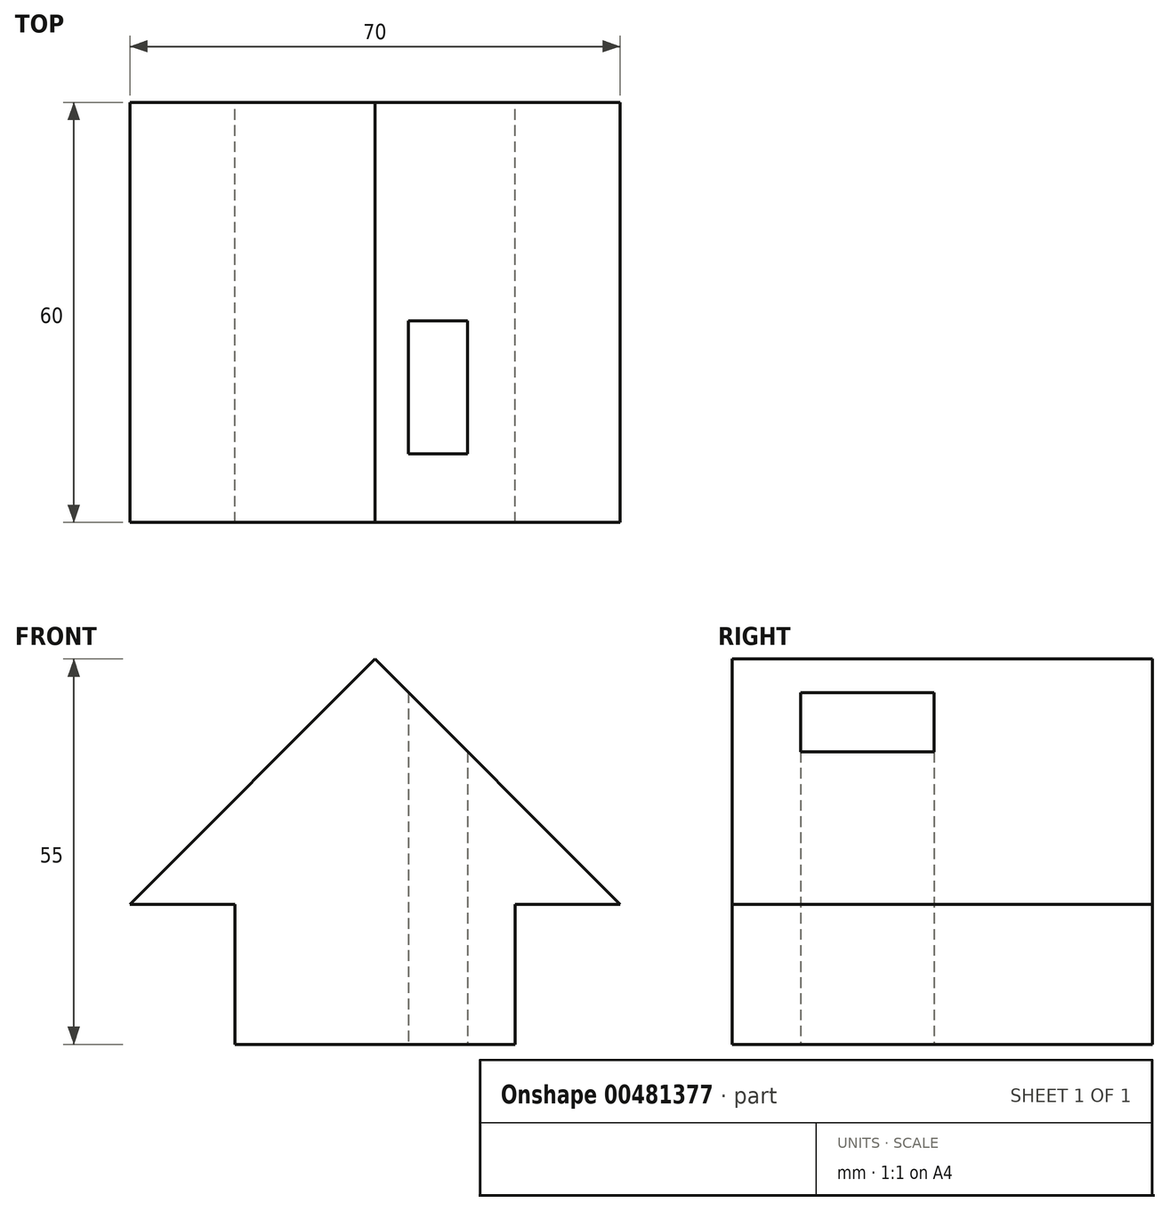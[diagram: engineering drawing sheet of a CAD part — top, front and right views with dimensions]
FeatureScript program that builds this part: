
annotation { "Feature Type Name" : "Feature", "Feature Type Description" : "" }
export const myFeature = defineFeature(function(context is Context, id is Id, definition is map)
    precondition{}
    {
        {
            var Q0;
            Q0=qCreatedBy(makeId("Front.planeOp"),FACE);
            var sketch = newSketch(context, id + "F0", { "sketchPlane" : qUnion([Q0])});
            skLineSegment(sketch, "E0", {"start": v(-20, 0) * mm, "end": v(20, 0) * mm});
            skLineSegment(sketch, "E1", {"start": v(20, 0) * mm, "end": v(20, 20) * mm});
            skLineSegment(sketch, "E2", {"start": v(20, 20) * mm, "end": v(35, 20) * mm});
            skLineSegment(sketch, "E3", {"start": v(35, 20) * mm, "end": v(0, 55) * mm});
            skLineSegment(sketch, "E4", {"start": v(0, 55) * mm, "end": v(-35, 20) * mm});
            skLineSegment(sketch, "E5", {"start": v(-35, 20) * mm, "end": v(-20, 20) * mm});
            skLineSegment(sketch, "E6", {"start": v(-20, 20) * mm, "end": v(-20, 0) * mm});
            skSolve(sketch);
        }
        {
            var Q0;
            Q0 = qSketchRegion(id + "F0", true);
            extrude(context, id + "F1", {"entities" : qUnion([Q0]), "depth" : 60 * mm});
        }
        {
            var Q0;
            Q0=makeQuery(id+"F1.opExtrude","SWEPT_FACE",FACE,{"disambiguationData":[OSD([sQuery(id+"F0.wireOp",EDGE,"E0")])]});
            var sketch = newSketch(context, id + "F2", { "sketchPlane" : qUnion([Q0])});
            skLineSegment(sketch, "E7.bottom", {"start": v(4.79, 31.2) * mm, "end": v(13.25, 31.2) * mm});
            skLineSegment(sketch, "E7.top", {"start": v(4.79, 50.22) * mm, "end": v(13.25, 50.22) * mm});
            skLineSegment(sketch, "E7.left", {"start": v(4.79, 31.2) * mm, "end": v(4.79, 50.22) * mm});
            skLineSegment(sketch, "E7.right", {"start": v(13.25, 31.2) * mm, "end": v(13.25, 50.22) * mm});
            skPoint(sketch, "E7.middle", {"position": v(9.02, 40.7) * mm});
            skSolve(sketch);
        }
        {
            var Q0;
            Q0=makeQuery(id+"F2.imprint","IMPRINT",FACE,{"disambiguationData":[TD([[makeQuery(id+"F2.imprint","IMPRINT",EDGE,{"derivedFrom":sQuery(id+"F2.wireOp",EDGE,"E7.bottom")}),1.0]])]});
            extrude(context, id + "F3", {"entities" : qUnion([Q0]), "operationType" : NewBodyOperationType.REMOVE, "oppositeDirection" : true, "depth" : 70 * mm});
        }
    });
